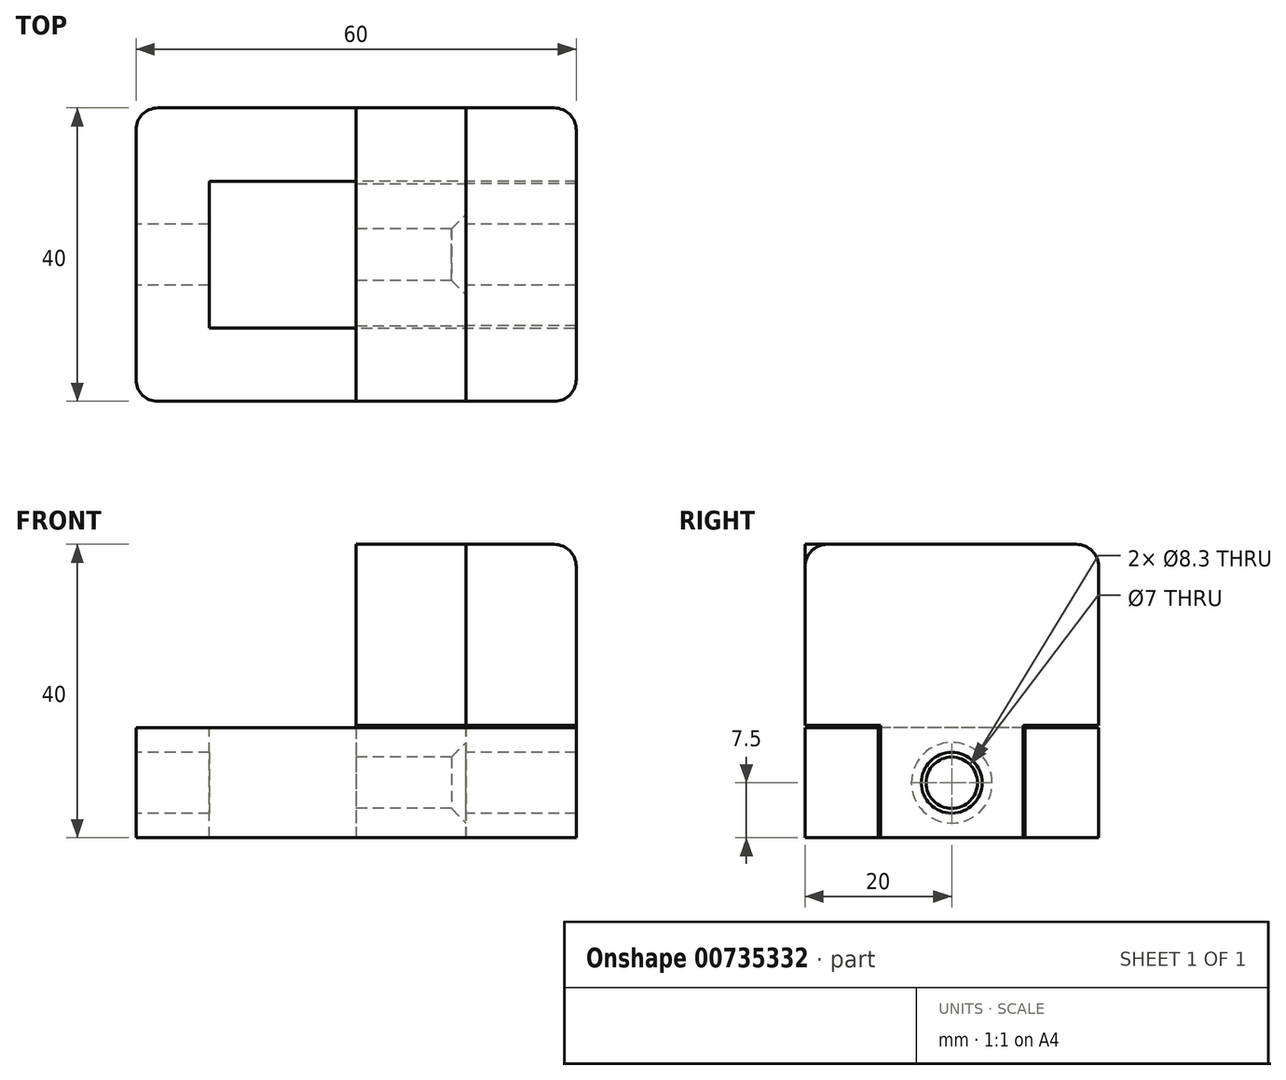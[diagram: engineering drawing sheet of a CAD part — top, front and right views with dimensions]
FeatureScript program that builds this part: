
annotation { "Feature Type Name" : "Feature", "Feature Type Description" : "" }
export const myFeature = defineFeature(function(context is Context, id is Id, definition is map)
    precondition{}
    {
        {
            var Q0;
            Q0=qCreatedBy(makeId("Top.planeOp"),FACE);
            var sketch = newSketch(context, id + "F0", { "sketchPlane" : qUnion([Q0])});
            skLineSegment(sketch, "E0.bottom", {"start": v(0, 20) * mm, "end": v(-60, 20) * mm});
            skLineSegment(sketch, "E0.top", {"start": v(0, -20) * mm, "end": v(-60, -20) * mm});
            skLineSegment(sketch, "E0.left", {"start": v(0, 20) * mm, "end": v(0, -20) * mm});
            skLineSegment(sketch, "E0.right", {"start": v(-60, 20) * mm, "end": v(-60, -20) * mm});
            skSolve(sketch);
        }
        {
            var Q0;
            Q0 = qSketchRegion(id + "F0", true);
            extrude(context, id + "F1", {"entities" : qUnion([Q0]), "depth" : 15 * mm, "offsetDistance" : 25 * mm});
        }
        {
            var Q0;
            Q0=makeQuery(id+"F1.opExtrude","CAP_FACE",FACE,{"disambiguationData":[OSD([sQuery(id+"F0.wireOp",EDGE,"E0.bottom"),sQuery(id+"F0.wireOp",EDGE,"E0.top"),sQuery(id+"F0.wireOp",EDGE,"E0.left"),sQuery(id+"F0.wireOp",EDGE,"E0.right")])],"isStart":false});
            var sketch = newSketch(context, id + "F2", { "sketchPlane" : qUnion([Q0])});
            skLineSegment(sketch, "E1.bottom", {"start": v(0, 20) * mm, "end": v(-15, 20) * mm});
            skLineSegment(sketch, "E1.top", {"start": v(0, -20) * mm, "end": v(-15, -20) * mm});
            skLineSegment(sketch, "E1.left", {"start": v(0, 20) * mm, "end": v(0, -20) * mm});
            skLineSegment(sketch, "E1.right", {"start": v(-15, 20) * mm, "end": v(-15, -20) * mm});
            skSolve(sketch);
        }
        {
            var Q0;
            Q0 = qSketchRegion(id + "F2", true);
            extrude(context, id + "F3", {"entities" : qUnion([Q0]), "operationType" : NewBodyOperationType.ADD, "depth" : 25 * mm, "offsetDistance" : 25 * mm});
        }
        {
            var Q0;
            Q0=makeQuery(id+"F1.opExtrude","CAP_FACE",FACE,{"disambiguationData":[OSD([sQuery(id+"F0.wireOp",EDGE,"E0.bottom"),sQuery(id+"F0.wireOp",EDGE,"E0.top"),sQuery(id+"F0.wireOp",EDGE,"E0.left"),sQuery(id+"F0.wireOp",EDGE,"E0.right")])],"isStart":false});
            var sketch = newSketch(context, id + "F4", { "sketchPlane" : qUnion([Q0])});
            skLineSegment(sketch, "E2.bottom", {"start": v(-50, 10) * mm, "end": v(-15, 10) * mm});
            skLineSegment(sketch, "E2.top", {"start": v(-50, -10) * mm, "end": v(-15, -10) * mm});
            skLineSegment(sketch, "E2.left", {"start": v(-50, 10) * mm, "end": v(-50, -10) * mm});
            skLineSegment(sketch, "E2.right", {"start": v(-15, 10) * mm, "end": v(-15, -10) * mm});
            skPoint(sketch, "E3", {"position": v(-15, 0) * mm});
            skSolve(sketch);
        }
        {
            var Q0;
            Q0 = qSketchRegion(id + "F4", true);
            extrude(context, id + "F5", {"entities" : qUnion([Q0]), "operationType" : NewBodyOperationType.REMOVE, "endBound" : BoundingType.THROUGH_ALL, "oppositeDirection" : true, "depth" : 25 * mm, "offsetDistance" : 25 * mm});
        }
        {
            var Q0;
            Q0=makeQuery(id+"F1.opExtrude","SWEPT_FACE",FACE,{"disambiguationData":[OSD([sQuery(id+"F0.wireOp",EDGE,"E0.right")])]});
            var sketch = newSketch(context, id + "F6", { "sketchPlane" : qUnion([Q0])});
            skCircle(sketch, "E4", {"center": v(0, 7.5) * mm, "radius": 4.15 * mm});
            skLineSegment(sketch, "E5", {"start": v(0, 15) * mm, "end": v(0, 0) * mm, "construction": true});
            skSolve(sketch);
        }
        {
            var Q0;
            Q0 = qSketchRegion(id + "F6", true);
            extrude(context, id + "F7", {"entities" : qUnion([Q0]), "operationType" : NewBodyOperationType.REMOVE, "endBound" : BoundingType.THROUGH_ALL, "oppositeDirection" : true, "depth" : 25 * mm, "offsetDistance" : 25 * mm});
        }
        {
            var Q0;
            Q0=makeQuery(id+"F5.boolean.opBoolean","MERGE",FACE,{"derivedFrom":[makeQuery(id+"F3.opExtrude","SWEPT_FACE",FACE,{"disambiguationData":[OSD([sQuery(id+"F2.wireOp",EDGE,"E1.right")])]}),makeQuery(id+"F5.opExtrude","SWEPT_FACE",FACE,{"disambiguationData":[OSD([sQuery(id+"F4.wireOp",EDGE,"E2.right")])]})]});
            var sketch = newSketch(context, id + "F8", { "sketchPlane" : qUnion([Q0])});
            skLineSegment(sketch, "E6.0", {"start": v(-20, 40) * mm, "end": v(20, 40) * mm});
            skLineSegment(sketch, "E7.0", {"start": v(20, 40) * mm, "end": v(20, 15) * mm});
            skLineSegment(sketch, "E8.0.0", {"start": v(-20, 15) * mm, "end": v(-10, 15) * mm});
            skLineSegment(sketch, "E8.0.1", {"start": v(-10, 15) * mm, "end": v(-10, 0) * mm});
            skLineSegment(sketch, "E8.0.2", {"start": v(-10, 0) * mm, "end": v(10, 0) * mm});
            skLineSegment(sketch, "E8.0.3", {"start": v(10, 0) * mm, "end": v(10, 15) * mm});
            skLineSegment(sketch, "E8.0.4", {"start": v(10, 15) * mm, "end": v(20, 15) * mm});
            skLineSegment(sketch, "E8.0.5", {"start": v(20, 15) * mm, "end": v(20, 40) * mm});
            skLineSegment(sketch, "E8.0.6", {"start": v(20, 40) * mm, "end": v(-20, 40) * mm});
            skLineSegment(sketch, "E8.0.7", {"start": v(-20, 40) * mm, "end": v(-20, 15) * mm});
            skSolve(sketch);
        }
        {
            var Q0;
            Q0 = qSketchRegion(id + "F8", true);
            extrude(context, id + "F9", {"entities" : qUnion([Q0]), "depth" : 15 * mm, "offsetDistance" : 25 * mm});
        }
        {
            var Q0;
            Q0=makeQuery(id+"F9.opExtrude","CAP_FACE",FACE,{"disambiguationData":[OSD([sQuery(id+"F8.wireOp",EDGE,"E8.0.0"),sQuery(id+"F8.wireOp",EDGE,"E8.0.1"),sQuery(id+"F8.wireOp",EDGE,"E8.0.2"),sQuery(id+"F8.wireOp",EDGE,"E8.0.3"),sQuery(id+"F8.wireOp",EDGE,"E8.0.4"),sQuery(id+"F8.wireOp",EDGE,"E8.0.5"),sQuery(id+"F8.wireOp",EDGE,"E8.0.6"),sQuery(id+"F8.wireOp",EDGE,"E8.0.7")])],"isStart":false});
            var sketch = newSketch(context, id + "F10", { "sketchPlane" : qUnion([Q0])});
            skLineSegment(sketch, "E9", {"start": v(0, 0) * mm, "end": v(0, 19.18) * mm, "construction": true});
            skLineSegment(sketch, "E10", {"start": v(-20, 15.3) * mm, "end": v(-9.7, 15.3) * mm});
            skLineSegment(sketch, "E11", {"start": v(-9.7, 15.3) * mm, "end": v(-9.7, 0) * mm});
            skLineSegment(sketch, "E12", {"start": v(-9.7, 0) * mm, "end": v(-10, 0) * mm});
            skLineSegment(sketch, "E13", {"start": v(-10, 0) * mm, "end": v(-10, 15) * mm});
            skLineSegment(sketch, "E14", {"start": v(-10, 15) * mm, "end": v(-20, 15) * mm});
            skLineSegment(sketch, "E15", {"start": v(-20, 15) * mm, "end": v(-20, 15.3) * mm});
            skLineSegment(sketch, "E16.MirrorCS", {"start": v(9.7, 0) * mm, "end": v(10, 0) * mm});
            skLineSegment(sketch, "E17.MirrorCS", {"start": v(20, 15) * mm, "end": v(20, 15.3) * mm});
            skLineSegment(sketch, "E18.MirrorCS", {"start": v(10, 0) * mm, "end": v(10, 15) * mm});
            skLineSegment(sketch, "E19.MirrorCS", {"start": v(10, 15) * mm, "end": v(20, 15) * mm});
            skLineSegment(sketch, "E20.MirrorCS", {"start": v(9.7, 15.3) * mm, "end": v(9.7, 0) * mm});
            skLineSegment(sketch, "E21.MirrorCS", {"start": v(20, 15.3) * mm, "end": v(9.7, 15.3) * mm});
            skSolve(sketch);
        }
        {
            var Q0;
            Q0 = qSketchRegion(id + "F10", true);
            extrude(context, id + "F11", {"entities" : qUnion([Q0]), "operationType" : NewBodyOperationType.REMOVE, "endBound" : BoundingType.THROUGH_ALL, "oppositeDirection" : true, "depth" : 25 * mm, "offsetDistance" : 25 * mm});
        }
        {
            var Q0;
            Q0=makeQuery(id+"F9.opExtrude","CAP_FACE",FACE,{"disambiguationData":[OSD([sQuery(id+"F8.wireOp",EDGE,"E8.0.0"),sQuery(id+"F8.wireOp",EDGE,"E8.0.1"),sQuery(id+"F8.wireOp",EDGE,"E8.0.2"),sQuery(id+"F8.wireOp",EDGE,"E8.0.3"),sQuery(id+"F8.wireOp",EDGE,"E8.0.4"),sQuery(id+"F8.wireOp",EDGE,"E8.0.5"),sQuery(id+"F8.wireOp",EDGE,"E8.0.6"),sQuery(id+"F8.wireOp",EDGE,"E8.0.7")])],"isStart":false});
            var sketch = newSketch(context, id + "F12", { "sketchPlane" : qUnion([Q0])});
            skPoint(sketch, "E22", {"position": v(0, 7.5) * mm});
            skCircle(sketch, "E23", {"center": v(0, 7.5) * mm, "radius": 3.5 * mm});
            skSolve(sketch);
        }
        {
            var Q0;
            Q0 = qSketchRegion(id + "F12", true);
            extrude(context, id + "F13", {"entities" : qUnion([Q0]), "operationType" : NewBodyOperationType.REMOVE, "endBound" : BoundingType.THROUGH_ALL, "oppositeDirection" : true, "depth" : 25 * mm, "offsetDistance" : 25 * mm});
        }
        {
            var Q0;
            Q0=makeQuery(id+"F13.boolean.opBoolean","COPY",EDGE,{"derivedFrom":makeQuery(id+"F13.opExtrude","CAP_EDGE",EDGE,{"disambiguationData":[OSD([sQuery(id+"F12.wireOp",EDGE,"E23")])],"isStart":true})});
            var Q1;
            Q1=makeQuery(id+"F13.boolean.opBoolean","INTERSECT",EDGE,{"derivedFrom":[makeQuery(id+"F9.opExtrude","CAP_FACE",FACE,{"disambiguationData":[OSD([sQuery(id+"F8.wireOp",EDGE,"E8.0.0"),sQuery(id+"F8.wireOp",EDGE,"E8.0.1"),sQuery(id+"F8.wireOp",EDGE,"E8.0.2"),sQuery(id+"F8.wireOp",EDGE,"E8.0.3"),sQuery(id+"F8.wireOp",EDGE,"E8.0.4"),sQuery(id+"F8.wireOp",EDGE,"E8.0.5"),sQuery(id+"F8.wireOp",EDGE,"E8.0.6"),sQuery(id+"F8.wireOp",EDGE,"E8.0.7")])],"isStart":true}),makeQuery(id+"F13.opExtrude","SWEPT_FACE",FACE,{"disambiguationData":[OSD([sQuery(id+"F12.wireOp",EDGE,"E23")])]})]});
            chamfer(context, id + "F14", {"entities" : qUnion([Q0, Q1]), "width" : 2 * mm, "tangentPropagation" : true});
        }
        {
            var Q0;
            Q0=makeQuery(id+"F3.boolean.opBoolean","MERGE",EDGE,{"derivedFrom":[makeQuery(id+"F1.opExtrude","SWEPT_EDGE",EDGE,{"disambiguationData":[OSD([sQuery(id+"F0.wireOp",EDGE,"E0.top"),sQuery(id+"F0.wireOp",EDGE,"E0.left")])]}),makeQuery(id+"F3.opExtrude","SWEPT_EDGE",EDGE,{"disambiguationData":[OSD([sQuery(id+"F2.wireOp",EDGE,"E1.top"),sQuery(id+"F2.wireOp",EDGE,"E1.left")])]})]});
            var Q1;
            Q1=makeQuery(id+"F3.opExtrude","CAP_EDGE",EDGE,{"disambiguationData":[OSD([sQuery(id+"F2.wireOp",EDGE,"E1.top")])],"isStart":false});
            var Q2;
            Q2=makeQuery(id+"F3.opExtrude","CAP_EDGE",EDGE,{"disambiguationData":[OSD([sQuery(id+"F2.wireOp",EDGE,"E1.left")])],"isStart":false});
            var Q3;
            Q3=makeQuery(id+"F3.boolean.opBoolean","MERGE",EDGE,{"derivedFrom":[makeQuery(id+"F1.opExtrude","SWEPT_EDGE",EDGE,{"disambiguationData":[OSD([sQuery(id+"F0.wireOp",EDGE,"E0.bottom"),sQuery(id+"F0.wireOp",EDGE,"E0.left")])]}),makeQuery(id+"F3.opExtrude","SWEPT_EDGE",EDGE,{"disambiguationData":[OSD([sQuery(id+"F2.wireOp",EDGE,"E1.bottom"),sQuery(id+"F2.wireOp",EDGE,"E1.left")])]})]});
            var Q4;
            Q4=makeQuery(id+"F3.opExtrude","CAP_EDGE",EDGE,{"disambiguationData":[OSD([sQuery(id+"F2.wireOp",EDGE,"E1.bottom")])],"isStart":false});
            var Q5;
            Q5=makeQuery(id+"F9.opExtrude","SWEPT_EDGE",EDGE,{"disambiguationData":[OSD([sQuery(id+"F8.wireOp",EDGE,"E8.0.5"),sQuery(id+"F8.wireOp",EDGE,"E8.0.6")])]});
            var Q6;
            Q6=makeQuery(id+"F9.opExtrude","SWEPT_EDGE",EDGE,{"disambiguationData":[OSD([sQuery(id+"F8.wireOp",EDGE,"E8.0.6"),sQuery(id+"F8.wireOp",EDGE,"E8.0.7")])]});
            var Q7;
            Q7=makeQuery(id+"F1.opExtrude","SWEPT_EDGE",EDGE,{"disambiguationData":[OSD([sQuery(id+"F0.wireOp",EDGE,"E0.top"),sQuery(id+"F0.wireOp",EDGE,"E0.right")])]});
            var Q8;
            Q8=makeQuery(id+"F1.opExtrude","SWEPT_EDGE",EDGE,{"disambiguationData":[OSD([sQuery(id+"F0.wireOp",EDGE,"E0.bottom"),sQuery(id+"F0.wireOp",EDGE,"E0.right")])]});
            var Q9;
            Q9=makeQuery(id+"F5.boolean.opBoolean","COPY",EDGE,{"derivedFrom":makeQuery(id+"F5.opExtrude","CAP_EDGE",EDGE,{"disambiguationData":[OSD([sQuery(id+"F4.wireOp",EDGE,"E2.top")])],"isStart":true})});
            var Q10;
            Q10=makeQuery(id+"F5.boolean.opBoolean","COPY",EDGE,{"derivedFrom":makeQuery(id+"F5.opExtrude","CAP_EDGE",EDGE,{"disambiguationData":[OSD([sQuery(id+"F4.wireOp",EDGE,"E2.bottom")])],"isStart":true})});
            fillet(context, id + "F15", {"entities" : qUnion([Q0, Q1, Q2, Q3, Q4, Q5, Q6, Q7, Q8, Q9, Q10]), "radius" : 3 * mm, "tangentPropagation" : true, "allowEdgeOverflow" : false});
        }
    });
